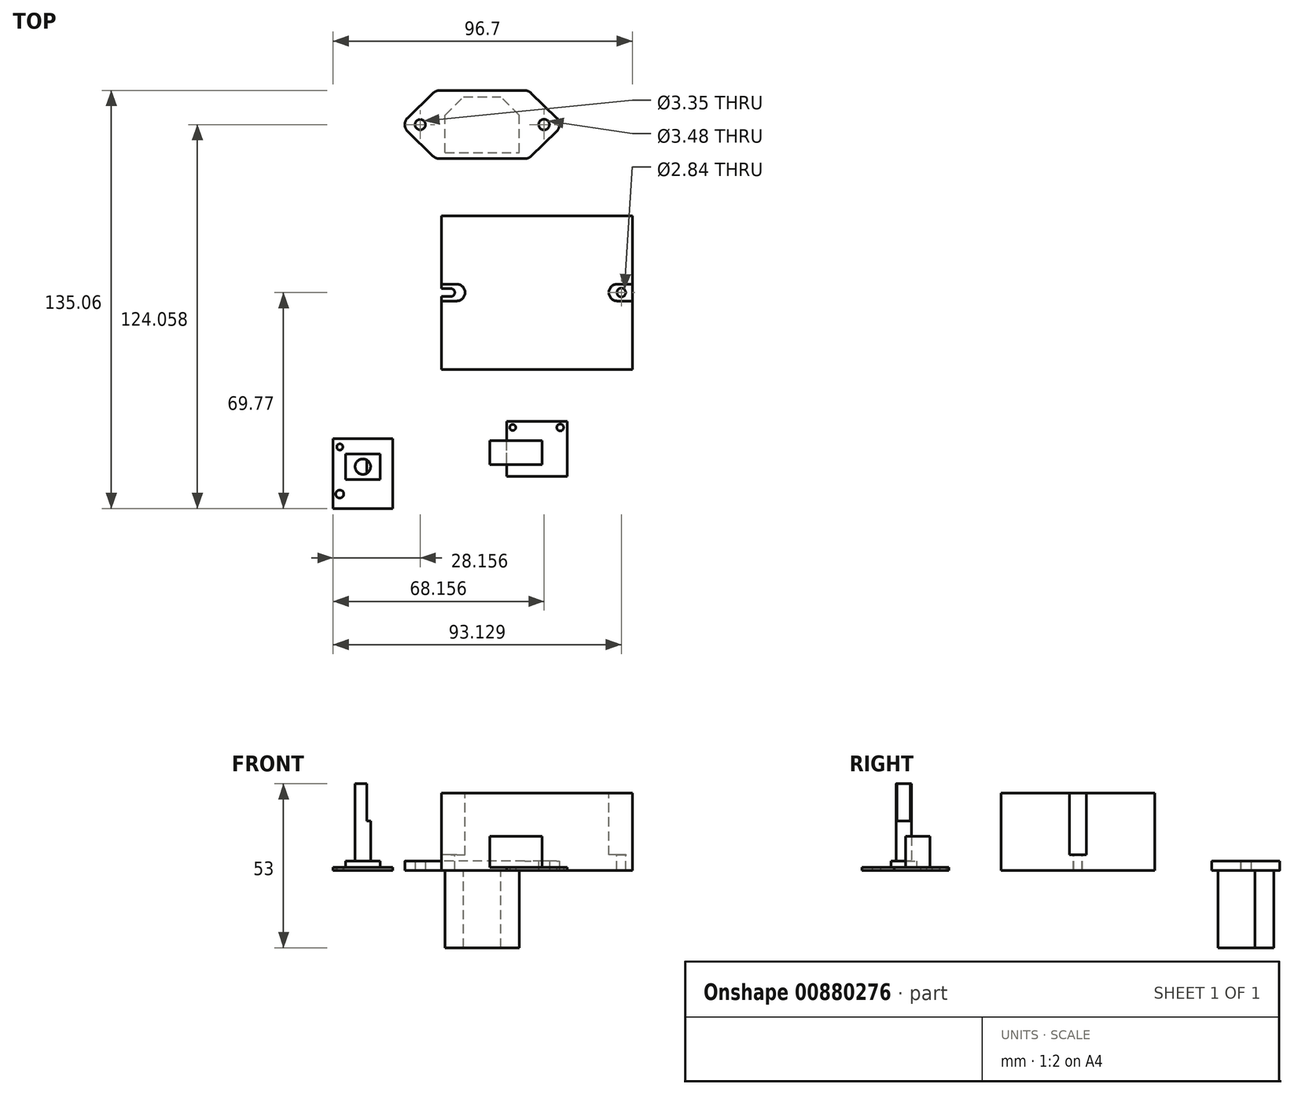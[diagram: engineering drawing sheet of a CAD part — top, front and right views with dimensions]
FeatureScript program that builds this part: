
annotation { "Feature Type Name" : "Feature", "Feature Type Description" : "" }
export const myFeature = defineFeature(function(context is Context, id is Id, definition is map)
    precondition{}
    {
        {
            var Q0;
            Q0=qCreatedBy(makeId("Top.planeOp"),FACE);
            var sketch = newSketch(context, id + "F0", { "sketchPlane" : qUnion([Q0])});
            skLineSegment(sketch, "E0.bottom", {"start": v(30.83, 24.82) * mm, "end": v(-30.83, 24.82) * mm});
            skLineSegment(sketch, "E0.top", {"start": v(30.83, -24.82) * mm, "end": v(-30.83, -24.82) * mm});
            skLineSegment(sketch, "E0.left", {"start": v(30.83, 24.82) * mm, "end": v(30.83, -24.82) * mm});
            skLineSegment(sketch, "E0.right", {"start": v(-30.83, 24.82) * mm, "end": v(-30.83, -24.82) * mm});
            skPoint(sketch, "E0.middle", {"position": v(0, 0) * mm});
            skSolve(sketch);
        }
        {
            var Q0;
            Q0=makeQuery(id+"F0.imprint","IMPRINT",FACE,{"disambiguationData":[TD([[makeQuery(id+"F0.imprint","IMPRINT",EDGE,{"derivedFrom":sQuery(id+"F0.wireOp",EDGE,"E0.bottom")}),1.0]])]});
            extrude(context, id + "F1", {"entities" : qUnion([Q0]), "depth" : 25 * mm, "offsetDistance" : 25 * mm});
        }
        {
            var Q0;
            Q0=makeQuery(id+"F1.opExtrude","CAP_FACE",FACE,{"disambiguationData":[OSD([sQuery(id+"F0.wireOp",EDGE,"E0.bottom"),sQuery(id+"F0.wireOp",EDGE,"E0.top"),sQuery(id+"F0.wireOp",EDGE,"E0.left"),sQuery(id+"F0.wireOp",EDGE,"E0.right")])],"isStart":false});
            var sketch = newSketch(context, id + "F2", { "sketchPlane" : qUnion([Q0])});
            skArc(sketch, "E1", {"start": v(-25.96, -2.72) * mm, "mid": v(-23.25, 0) * mm, "end": v(-25.96, 2.72) * mm});
            skLineSegment(sketch, "E2.bottom", {"start": v(-25.96, 2.72) * mm, "end": v(-48.54, 2.72) * mm});
            skLineSegment(sketch, "E2.top", {"start": v(-25.96, -2.72) * mm, "end": v(-48.54, -2.72) * mm});
            skLineSegment(sketch, "E2.right", {"start": v(-48.54, 2.72) * mm, "end": v(-48.54, -2.72) * mm});
            skPoint(sketch, "E2.middle", {"position": v(-37.25, 0) * mm});
            skLineSegment(sketch, "E3.MirrorCS", {"start": v(48.54, 2.72) * mm, "end": v(48.54, -2.72) * mm});
            skArc(sketch, "E4.MirrorCS", {"start": v(25.96, -2.72) * mm, "mid": v(23.25, 0) * mm, "end": v(25.96, 2.72) * mm});
            skLineSegment(sketch, "E5.MirrorCS", {"start": v(25.96, -2.72) * mm, "end": v(48.54, -2.72) * mm});
            skLineSegment(sketch, "E6.MirrorCS", {"start": v(25.96, 2.72) * mm, "end": v(48.54, 2.72) * mm});
            skPoint(sketch, "E7.MirrorP", {"position": v(37.25, 0) * mm});
            skSolve(sketch);
        }
        {
            var Q0;
            Q0 = qSketchRegion(id + "F2", true);
            extrude(context, id + "F3", {"entities" : qUnion([Q0]), "operationType" : NewBodyOperationType.REMOVE, "oppositeDirection" : true, "depth" : 20 * mm, "offsetDistance" : 25 * mm});
        }
        {
            var Q0;
            Q0=makeQuery(id+"F3.boolean.opBoolean","COPY",FACE,{"derivedFrom":makeQuery(id+"F3.opExtrude","CAP_FACE",FACE,{"disambiguationData":[OSD([sQuery(id+"F2.wireOp",EDGE,"E1"),sQuery(id+"F2.wireOp",EDGE,"E2.bottom"),sQuery(id+"F2.wireOp",EDGE,"E2.top"),sQuery(id+"F2.wireOp",EDGE,"E2.right")])],"isStart":false})});
            var sketch = newSketch(context, id + "F4", { "sketchPlane" : qUnion([Q0])});
            skCircle(sketch, "E8", {"center": v(27.26, 0) * mm, "radius": 1.42 * mm});
            skArc(sketch, "E9", {"start": v(-27.86, -1.29) * mm, "mid": v(-26.58, 0) * mm, "end": v(-27.86, 1.29) * mm});
            skLineSegment(sketch, "E10.bottom", {"start": v(-27.86, 1.29) * mm, "end": v(-35.78, 1.29) * mm});
            skLineSegment(sketch, "E10.top", {"start": v(-27.86, -1.29) * mm, "end": v(-35.78, -1.29) * mm});
            skLineSegment(sketch, "E10.right", {"start": v(-35.78, 1.29) * mm, "end": v(-35.78, -1.29) * mm});
            skPoint(sketch, "E10.middle", {"position": v(-31.82, 0) * mm});
            skSolve(sketch);
        }
        {
            var Q0;
            {var subQ0=sQuery(id+"F4.wireOp",EDGE,"E9");Q0=makeQuery(id+"F4.imprint","IMPRINT",FACE,{"disambiguationData":[TD([[makeQuery(id+"F4.imprint","IMPRINT",EDGE,{"derivedFrom":subQ0}),1.0]])]});}
            var Q1;
            Q1=makeQuery(id+"F4.imprint","IMPRINT",FACE,{"disambiguationData":[TD([[makeQuery(id+"F4.imprint","IMPRINT",EDGE,{"derivedFrom":sQuery(id+"F4.wireOp",EDGE,"E8")}),1.0]])]});
            extrude(context, id + "F5", {"entities" : qUnion([Q0, Q1]), "operationType" : NewBodyOperationType.REMOVE, "oppositeDirection" : true, "depth" : 25 * mm, "offsetDistance" : 25 * mm});
        }
        {
            var Q0;
            Q0=qCreatedBy(makeId("Top.planeOp"),FACE);
            var sketch = newSketch(context, id + "F6", { "sketchPlane" : qUnion([Q0])});
            skLineSegment(sketch, "E11.bottom", {"start": v(-9.79, -59.38) * mm, "end": v(9.79, -59.38) * mm});
            skLineSegment(sketch, "E11.top", {"start": v(-9.79, -41.66) * mm, "end": v(9.79, -41.66) * mm});
            skLineSegment(sketch, "E11.left", {"start": v(-9.79, -59.38) * mm, "end": v(-9.79, -41.66) * mm});
            skLineSegment(sketch, "E11.right", {"start": v(9.79, -59.38) * mm, "end": v(9.79, -41.66) * mm});
            skPoint(sketch, "E11.middle", {"position": v(0, -50.52) * mm});
            skCircle(sketch, "E12", {"center": v(7.5, -43.62) * mm, "radius": 1.11 * mm});
            skCircle(sketch, "E13", {"center": v(-7.83, -43.62) * mm, "radius": 0.97 * mm});
            skSolve(sketch);
        }
        {
            var Q0;
            Q0=makeQuery(id+"F6.imprint","IMPRINT",FACE,{"disambiguationData":[TD([[makeQuery(id+"F6.imprint","IMPRINT",EDGE,{"derivedFrom":sQuery(id+"F6.wireOp",EDGE,"E11.bottom")}),1.0]])]});
            extrude(context, id + "F7", {"entities" : qUnion([Q0]), "depth" : 1 * mm, "offsetDistance" : 25 * mm});
        }
        {
            var Q0;
            Q0=makeQuery(id+"F7.opExtrude","CAP_FACE",FACE,{"disambiguationData":[OSD([sQuery(id+"F6.wireOp",EDGE,"E11.bottom"),sQuery(id+"F6.wireOp",EDGE,"E11.top"),sQuery(id+"F6.wireOp",EDGE,"E11.left"),sQuery(id+"F6.wireOp",EDGE,"E11.right"),sQuery(id+"F6.wireOp",EDGE,"E12"),sQuery(id+"F6.wireOp",EDGE,"E13")])],"isStart":false});
            var sketch = newSketch(context, id + "F8", { "sketchPlane" : qUnion([Q0])});
            skLineSegment(sketch, "E14.bottom", {"start": v(-15.18, -47.8) * mm, "end": v(1.7, -47.8) * mm});
            skLineSegment(sketch, "E14.top", {"start": v(-15.18, -55.65) * mm, "end": v(1.7, -55.65) * mm});
            skLineSegment(sketch, "E14.left", {"start": v(-15.18, -47.8) * mm, "end": v(-15.18, -55.65) * mm});
            skLineSegment(sketch, "E14.right", {"start": v(1.7, -47.8) * mm, "end": v(1.7, -55.65) * mm});
            skSolve(sketch);
        }
        {
            var Q0;
            {var subQ0=sQuery(id+"F8.wireOp",EDGE,"E14.left");Q0=makeQuery(id+"F8.imprint","IMPRINT",FACE,{"disambiguationData":[TD([[makeQuery(id+"F8.imprint","IMPRINT",EDGE,{"derivedFrom":subQ0}),1.0]])]});}
            var Q1;
            {var subQ0=sQuery(id+"F8.wireOp",EDGE,"E14.right");Q1=makeQuery(id+"F8.imprint","IMPRINT",FACE,{"disambiguationData":[TD([[makeQuery(id+"F8.imprint","IMPRINT",EDGE,{"derivedFrom":subQ0}),-1.0]])]});}
            extrude(context, id + "F9", {"entities" : qUnion([Q0, Q1]), "operationType" : NewBodyOperationType.ADD, "depth" : 10 * mm, "offsetDistance" : 25 * mm});
        }
        {
            var Q0;
            Q0=qCreatedBy(makeId("Top.planeOp"),FACE);
            var sketch = newSketch(context, id + "F10", { "sketchPlane" : qUnion([Q0])});
            skLineSegment(sketch, "E15.bottom", {"start": v(-65.87, -69.77) * mm, "end": v(-46.66, -69.77) * mm});
            skLineSegment(sketch, "E15.top", {"start": v(-65.87, -47.2) * mm, "end": v(-46.66, -47.2) * mm});
            skLineSegment(sketch, "E15.left", {"start": v(-65.87, -69.77) * mm, "end": v(-65.87, -47.2) * mm});
            skLineSegment(sketch, "E15.right", {"start": v(-46.66, -69.77) * mm, "end": v(-46.66, -47.2) * mm});
            skCircle(sketch, "E16", {"center": v(-63.7, -49.9) * mm, "radius": 1 * mm});
            skCircle(sketch, "E17", {"center": v(-63.74, -65.12) * mm, "radius": 1.3 * mm});
            skSolve(sketch);
        }
        {
            var Q0;
            Q0=makeQuery(id+"F10.imprint","IMPRINT",FACE,{"disambiguationData":[TD([[makeQuery(id+"F10.imprint","IMPRINT",EDGE,{"derivedFrom":sQuery(id+"F10.wireOp",EDGE,"E15.bottom")}),1.0]])]});
            extrude(context, id + "F11", {"entities" : qUnion([Q0]), "depth" : 1 * mm, "offsetDistance" : 25 * mm});
        }
        {
            var Q0;
            Q0=qCreatedBy(makeId("Top.planeOp"),FACE);
            var sketch = newSketch(context, id + "F12", { "sketchPlane" : qUnion([Q0])});
            skLineSegment(sketch, "E18.bottom", {"start": v(-50.64, -60.4) * mm, "end": v(-61.88, -60.4) * mm});
            skLineSegment(sketch, "E18.top", {"start": v(-50.64, -52.14) * mm, "end": v(-61.88, -52.14) * mm});
            skLineSegment(sketch, "E18.left", {"start": v(-50.64, -60.4) * mm, "end": v(-50.64, -52.14) * mm});
            skLineSegment(sketch, "E18.right", {"start": v(-61.88, -60.4) * mm, "end": v(-61.88, -52.14) * mm});
            skPoint(sketch, "E18.middle", {"position": v(-56.26, -56.27) * mm});
            skSolve(sketch);
        }
        {
            var Q0;
            Q0 = qSketchRegion(id + "F12", true);
            extrude(context, id + "F13", {"entities" : qUnion([Q0]), "operationType" : NewBodyOperationType.ADD, "depth" : 3 * mm, "offsetDistance" : 25 * mm});
        }
        {
            var Q0;
            Q0=makeQuery(id+"F13.opExtrude","CAP_FACE",FACE,{"disambiguationData":[OSD([sQuery(id+"F12.wireOp",EDGE,"E18.bottom"),sQuery(id+"F12.wireOp",EDGE,"E18.top"),sQuery(id+"F12.wireOp",EDGE,"E18.left"),sQuery(id+"F12.wireOp",EDGE,"E18.right")])],"isStart":false});
            var sketch = newSketch(context, id + "F14", { "sketchPlane" : qUnion([Q0])});
            skCircle(sketch, "E19", {"center": v(-56.26, -56.27) * mm, "radius": 2.5 * mm});
            skLineSegment(sketch, "E20", {"start": v(-61.88, -52.14) * mm, "end": v(-50.64, -60.4) * mm, "construction": true});
            skLineSegment(sketch, "E21", {"start": v(-50.64, -52.14) * mm, "end": v(-61.88, -60.4) * mm, "construction": true});
            skSolve(sketch);
        }
        {
            var Q0;
            Q0 = qSketchRegion(id + "F14", true);
            extrude(context, id + "F15", {"entities" : qUnion([Q0]), "operationType" : NewBodyOperationType.ADD, "depth" : 25 * mm, "offsetDistance" : 25 * mm});
        }
        {
            var Q0;
            Q0=makeQuery(id+"F15.opExtrude","CAP_FACE",FACE,{"disambiguationData":[OSD([sQuery(id+"F14.wireOp",EDGE,"E19")])],"isStart":false});
            var sketch = newSketch(context, id + "F16", { "sketchPlane" : qUnion([Q0])});
            skLineSegment(sketch, "E22.bottom", {"start": v(-54.97, -53.2) * mm, "end": v(-52.7, -53.2) * mm});
            skLineSegment(sketch, "E22.top", {"start": v(-54.97, -59.38) * mm, "end": v(-52.7, -59.38) * mm});
            skLineSegment(sketch, "E22.left", {"start": v(-54.97, -53.2) * mm, "end": v(-54.97, -59.38) * mm});
            skLineSegment(sketch, "E22.right", {"start": v(-52.7, -53.2) * mm, "end": v(-52.7, -59.38) * mm});
            skSolve(sketch);
        }
        {
            var Q0;
            Q0 = qSketchRegion(id + "F16", true);
            extrude(context, id + "F17", {"entities" : qUnion([Q0]), "operationType" : NewBodyOperationType.REMOVE, "oppositeDirection" : true, "depth" : 12 * mm, "offsetDistance" : 25 * mm});
        }
        {
            var Q0;
            Q0=qCreatedBy(makeId("Top.planeOp"),FACE);
            var sketch = newSketch(context, id + "F18", { "sketchPlane" : qUnion([Q0])});
            skLineSegment(sketch, "E23.bottom", {"start": v(-3.93, 43.29) * mm, "end": v(-31.5, 43.29) * mm});
            skLineSegment(sketch, "E23.top", {"start": v(-3.93, 65.29) * mm, "end": v(-31.5, 65.29) * mm});
            skLineSegment(sketch, "E23.left", {"start": v(-2.71, 43.29) * mm, "end": v(-2.71, 43.55) * mm});
            skLineSegment(sketch, "E23.right", {"start": v(-32.71, 43.29) * mm, "end": v(-32.71, 43.55) * mm});
            skLineSegment(sketch, "E24", {"start": v(-55.98, 54.29) * mm, "end": v(50, 54.29) * mm, "construction": true});
            skLineSegment(sketch, "E25", {"start": v(-33.59, 64.44) * mm, "end": v(-41.8, 56.44) * mm});
            skLineSegment(sketch, "E26", {"start": v(-41.8, 52.14) * mm, "end": v(-33.59, 44.14) * mm});
            skLineSegment(sketch, "E27", {"start": v(-1.84, 64.44) * mm, "end": v(6.38, 56.44) * mm});
            skLineSegment(sketch, "E28", {"start": v(6.38, 52.14) * mm, "end": v(-1.84, 44.14) * mm});
            skCircle(sketch, "E29", {"center": v(-37.71, 54.29) * mm, "radius": 1.67 * mm});
            skCircle(sketch, "E30", {"center": v(2.29, 54.29) * mm, "radius": 1.74 * mm});
            skPoint(sketch, "E31.visualSharp", {"position": v(-44.02, 54.29) * mm});
            skArc(sketch, "E31.filletArc", {"start": v(-41.8, 56.44) * mm, "mid": v(-42.71, 54.29) * mm, "end": v(-41.8, 52.14) * mm});
            skPoint(sketch, "E32.visualSharp", {"position": v(8.59, 54.29) * mm});
            skArc(sketch, "E32.filletArc", {"start": v(6.38, 52.14) * mm, "mid": v(7.29, 54.29) * mm, "end": v(6.38, 56.44) * mm});
            skPoint(sketch, "E33.visualSharp", {"position": v(-32.71, 65.29) * mm});
            skArc(sketch, "E33.filletArc", {"start": v(-31.5, 65.29) * mm, "mid": v(-32.62, 65.07) * mm, "end": v(-33.59, 64.44) * mm});
            skPoint(sketch, "E34.visualSharp", {"position": v(-2.71, 65.29) * mm});
            skArc(sketch, "E34.filletArc", {"start": v(-1.84, 64.44) * mm, "mid": v(-2.8, 65.07) * mm, "end": v(-3.93, 65.29) * mm});
            skPoint(sketch, "E35.visualSharp", {"position": v(-2.71, 43.29) * mm});
            skArc(sketch, "E35.filletArc", {"start": v(-3.93, 43.29) * mm, "mid": v(-2.8, 43.5) * mm, "end": v(-1.84, 44.14) * mm});
            skPoint(sketch, "E36.visualSharp", {"position": v(-32.71, 43.29) * mm});
            skArc(sketch, "E36.filletArc", {"start": v(-33.59, 44.14) * mm, "mid": v(-32.62, 43.5) * mm, "end": v(-31.5, 43.29) * mm});
            skLineSegment(sketch, "E37.trimOffspring", {"start": v(-32.71, 65.03) * mm, "end": v(-32.71, 65.29) * mm});
            skLineSegment(sketch, "E38.trimOffspring", {"start": v(-2.71, 65.03) * mm, "end": v(-2.71, 65.29) * mm});
            skSolve(sketch);
        }
        {
            var Q0;
            {var subQ1=sQuery(id+"F18.wireOp",EDGE,"E23.bottom");Q0=makeQuery(id+"F18.imprint","IMPRINT",FACE,{"disambiguationData":[TD([[makeQuery(id+"F18.imprint","IMPRINT",EDGE,{"derivedFrom":subQ1}),-1.0]])]});}
            extrude(context, id + "F19", {"entities" : qUnion([Q0]), "depth" : 3 * mm, "offsetDistance" : 25 * mm});
        }
        {
            var Q0;
            Q0=makeQuery(id+"F19.opExtrude","CAP_FACE",FACE,{"disambiguationData":[OSD([sQuery(id+"F18.wireOp",EDGE,"E23.bottom"),sQuery(id+"F18.wireOp",EDGE,"E23.top"),sQuery(id+"F18.wireOp",EDGE,"E25"),sQuery(id+"F18.wireOp",EDGE,"E26"),sQuery(id+"F18.wireOp",EDGE,"E27"),sQuery(id+"F18.wireOp",EDGE,"E28"),sQuery(id+"F18.wireOp",EDGE,"E29"),sQuery(id+"F18.wireOp",EDGE,"E30"),sQuery(id+"F18.wireOp",EDGE,"E31.filletArc"),sQuery(id+"F18.wireOp",EDGE,"E32.filletArc"),sQuery(id+"F18.wireOp",EDGE,"E33.filletArc"),sQuery(id+"F18.wireOp",EDGE,"E34.filletArc"),sQuery(id+"F18.wireOp",EDGE,"E35.filletArc"),sQuery(id+"F18.wireOp",EDGE,"E36.filletArc")])],"isStart":true});
            var sketch = newSketch(context, id + "F20", { "sketchPlane" : qUnion([Q0])});
            skLineSegment(sketch, "E39", {"start": v(-17.71, -65.29) * mm, "end": v(-17.71, -43.29) * mm, "construction": true});
            skLineSegment(sketch, "E40", {"start": v(-17.71, -43.29) * mm, "end": v(-17.71, -45.29) * mm});
            skLineSegment(sketch, "E41", {"start": v(-17.71, -45.29) * mm, "end": v(-5.71, -45.29) * mm});
            skLineSegment(sketch, "E42", {"start": v(-5.71, -45.29) * mm, "end": v(-5.71, -57.29) * mm});
            skLineSegment(sketch, "E43", {"start": v(-5.71, -57.29) * mm, "end": v(-11.71, -63.29) * mm});
            skLineSegment(sketch, "E44", {"start": v(-11.71, -63.29) * mm, "end": v(-17.71, -63.29) * mm});
            skLineSegment(sketch, "E45.MirrorCS", {"start": v(-23.71, -63.29) * mm, "end": v(-17.71, -63.29) * mm});
            skLineSegment(sketch, "E46.MirrorCS", {"start": v(-29.71, -57.29) * mm, "end": v(-23.71, -63.29) * mm});
            skLineSegment(sketch, "E47.MirrorCS", {"start": v(-29.71, -45.29) * mm, "end": v(-29.71, -57.29) * mm});
            skLineSegment(sketch, "E48.MirrorCS", {"start": v(-17.71, -45.29) * mm, "end": v(-29.71, -45.29) * mm});
            skSolve(sketch);
        }
        {
            var Q0;
            Q0 = qSketchRegion(id + "F20", true);
            extrude(context, id + "F21", {"entities" : qUnion([Q0]), "operationType" : NewBodyOperationType.ADD, "depth" : 25 * mm, "offsetDistance" : 25 * mm});
        }
    });
